# Revit family: 2100.112 Rainhead Overflow Sump 530x350x330
name_source: partatom
category: Plumbing Fixtures
revit_build: Autodesk Revit 2016 (Build: 20150714_1515(x64)
units: mm (PartAtom-declared; Revit-internal decimal feet)

## family parameters
Always vertical = No
Cut with Voids When Loaded = No
OmniClass Number = 23.60.30.11
OmniClass Title = Pipework Products for General Use
Part Type = Normal
Room Calculation Point = No
Round Connector Dimension = Use Diameter
Shared = No
Work Plane-Based = No

## types (2) — shared parameters
CW Connection = No
CutOut Length = 395 mm  [stored 1.29593 ft]
DVW150 Nozzle Heigth = 154 mm  [stored 0.505249 ft]
DWV100 Nozzle Height = 244 mm  [stored 0.800525 ft]
Flow = 0.0 L/s
HW Connection = No
Left Edge Position = 355 mm
Left Edge Void Position = 352 mm
Left Tube End = 79 mm
Length = 528 mm
Manufacturer = Aquanight Industries Ltd
Material = Aquanight-Black
Model = 2100.113
Nozzles Distance = 180 mm
Pool Depth = 79 mm
Right Edge Position = 88 mm  [stored 0.288714 ft]
Right Edge Void Position = 85 mm
URL = www.aquaknight.co.nz
Vent Connection = No
Waste Connection = Yes
Width = 352 mm

## per-type parameters (varying)
| type | Connector Description | Connector Diameter | Connector Location | CutOut Width | Description |
| 530x350x240 DWV100 | DWV100 | 100 mm  [stored 0.328084 ft] | 199 mm  [stored 0.652887 ft] | 220 mm  [stored 0.721785 ft] | Membrane Rainhead 530x350x240 DWV100 DN100 |
| 530x350x240 DWV150 | DWV150 | 150 mm | 117 mm  [stored 0.383858 ft] | 225 mm  [stored 0.738189 ft] | Rainhead Overflow Sump 530x350X240 DWV150 DN150 |

note: [stored X ft] marks values corroborated as IEEE doubles in the binary element streams (Revit-internal decimal feet)

## geometry (parser evidence)
native form markers: Sweep x2
no freeform markers — native parametric forms only
